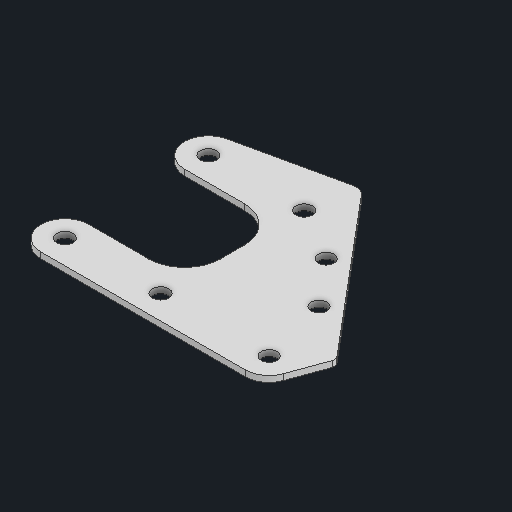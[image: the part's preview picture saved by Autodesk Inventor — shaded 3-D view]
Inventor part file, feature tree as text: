
AUTODESK INVENTOR PART (.ipt)
format: ipt  version: 2025 (Build 290162000, 162)  size: 146,944 bytes
history: native  units: in
note: dims shown in document units (in); Inventor stores cm internally (conversion verified against a paired STEP export)
features: other x6, sketch x1
ambient origin geometry x8: Origin, YZ Plane, XZ Plane, XY Plane, X Axis, Y Axis, Z Axis, Center Point
bodies: Solid1 (feature_tree)
feature tree (7):
  other  "funel_gusset.ipt"
  other  "Blocks"
  other  "main"
  other  "Solid1::funel_gusset.ipt"
  other  "TaggingFeature1"
  sketch  "Sketch1"  dims[d0=0.3937in d1=0.5in d6=0.375in d8=0.164in d9=0.0625in d14=0.164in d15=0.615in d17=0.125in]
  other  "main:1"
